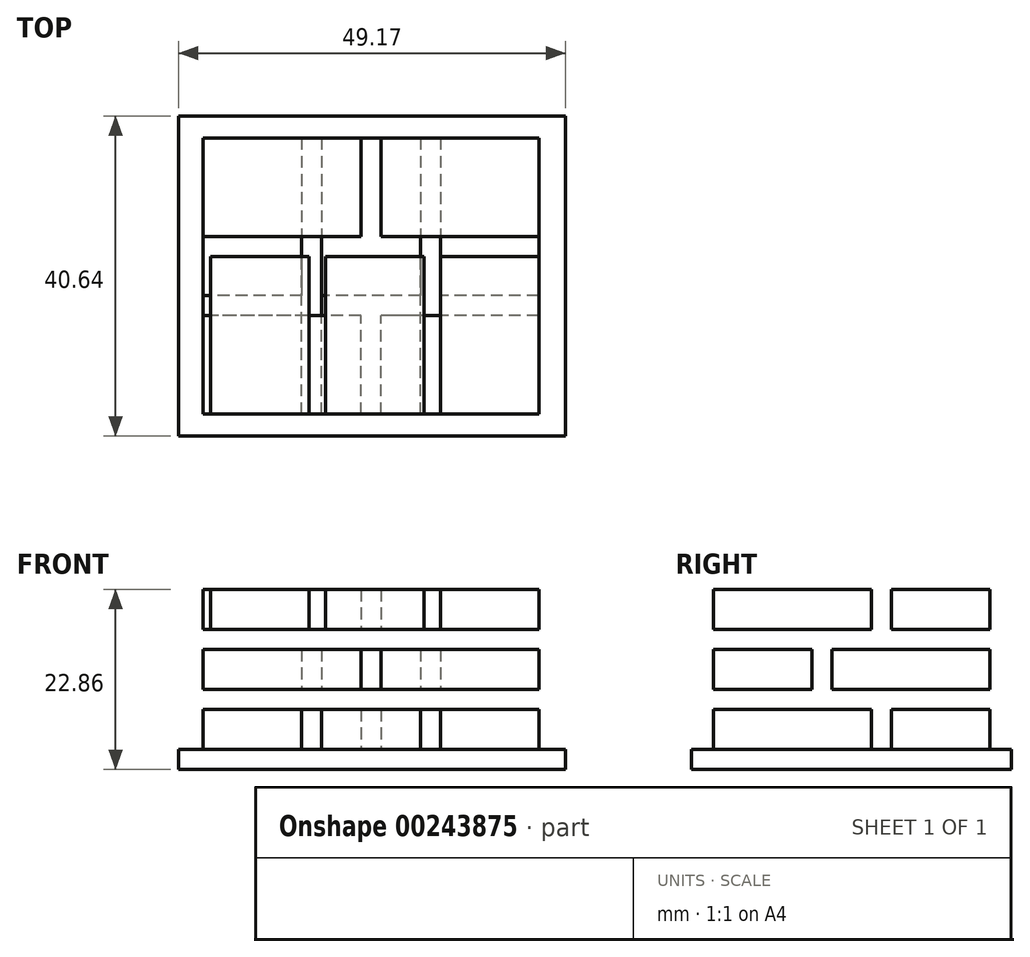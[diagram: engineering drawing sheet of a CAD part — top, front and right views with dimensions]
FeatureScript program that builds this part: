
annotation { "Feature Type Name" : "Feature", "Feature Type Description" : "" }
export const myFeature = defineFeature(function(context is Context, id is Id, definition is map)
    precondition{}
    {
        {
            var Q0;
            Q0=qCreatedBy(makeId("Top.planeOp"),FACE);
            var sketch = newSketch(context, id + "F0", { "sketchPlane" : qUnion([Q0])});
            skLineSegment(sketch, "E0.bottom", {"start": v(-21.31, 17.55) * mm, "end": v(-1.27, 17.55) * mm});
            skLineSegment(sketch, "E0.top", {"start": v(-21.31, 5.03) * mm, "end": v(-1.27, 5.03) * mm});
            skLineSegment(sketch, "E0.left", {"start": v(-21.31, 17.55) * mm, "end": v(-21.31, 5.03) * mm});
            skLineSegment(sketch, "E0.right", {"start": v(-1.27, 17.55) * mm, "end": v(-1.27, 5.03) * mm});
            skLineSegment(sketch, "E1.1.0.0", {"start": v(21.31, 17.55) * mm, "end": v(21.31, 5.03) * mm});
            skLineSegment(sketch, "E1.1.0.1", {"start": v(1.27, 17.55) * mm, "end": v(1.27, 5.03) * mm});
            skLineSegment(sketch, "E1.1.0.2", {"start": v(1.27, 5.03) * mm, "end": v(21.31, 5.03) * mm});
            skLineSegment(sketch, "E1.1.0.3", {"start": v(1.27, 17.55) * mm, "end": v(21.31, 17.55) * mm});
            skLineSegment(sketch, "E1.direction1", {"start": v(-21.31, 5.03) * mm, "end": v(1.27, 5.03) * mm, "construction": true});
            skLineSegment(sketch, "E2.bottom", {"start": v(-21.31, -17.55) * mm, "end": v(-21.31, 2.5) * mm});
            skLineSegment(sketch, "E2.top", {"start": v(-8.8, -17.55) * mm, "end": v(-8.8, 2.5) * mm});
            skLineSegment(sketch, "E2.left", {"start": v(-21.31, -17.55) * mm, "end": v(-8.8, -17.55) * mm});
            skLineSegment(sketch, "E2.right", {"start": v(-21.31, 2.5) * mm, "end": v(-8.8, 2.5) * mm});
            skLineSegment(sketch, "E3.1.0.0", {"start": v(-6.26, -17.55) * mm, "end": v(6.26, -17.55) * mm});
            skLineSegment(sketch, "E3.1.0.1", {"start": v(6.26, -17.55) * mm, "end": v(6.26, 2.5) * mm});
            skLineSegment(sketch, "E3.1.0.2", {"start": v(-6.26, -17.55) * mm, "end": v(-6.26, 2.5) * mm});
            skLineSegment(sketch, "E3.1.0.3", {"start": v(-6.26, 2.5) * mm, "end": v(6.26, 2.5) * mm});
            skLineSegment(sketch, "E3.2.0.0", {"start": v(8.8, -17.55) * mm, "end": v(21.31, -17.55) * mm});
            skLineSegment(sketch, "E3.2.0.1", {"start": v(21.31, -17.55) * mm, "end": v(21.31, 2.5) * mm});
            skLineSegment(sketch, "E3.2.0.2", {"start": v(8.8, -17.55) * mm, "end": v(8.8, 2.5) * mm});
            skLineSegment(sketch, "E3.2.0.3", {"start": v(8.8, 2.5) * mm, "end": v(21.31, 2.5) * mm});
            skLineSegment(sketch, "E3.direction1", {"start": v(-21.31, -17.55) * mm, "end": v(-6.26, -17.55) * mm, "construction": true});
            skLineSegment(sketch, "E4.bottom", {"start": v(-21.31, 17.55) * mm, "end": v(21.31, 17.55) * mm, "construction": true});
            skLineSegment(sketch, "E4.top", {"start": v(-21.31, -17.55) * mm, "end": v(21.31, -17.55) * mm, "construction": true});
            skLineSegment(sketch, "E4.left", {"start": v(-21.31, 17.55) * mm, "end": v(-21.31, -17.55) * mm, "construction": true});
            skLineSegment(sketch, "E4.right", {"start": v(21.31, 17.55) * mm, "end": v(21.31, -17.55) * mm, "construction": true});
            skSolve(sketch);
        }
        {
            var Q0;
            Q0=makeQuery(id+"F0.imprint","IMPRINT",FACE,{"disambiguationData":[TD([[makeQuery(id+"F0.imprint","IMPRINT",EDGE,{"derivedFrom":sQuery(id+"F0.wireOp",EDGE,"E1.1.0.0")}),-1.0]])]});
            var Q1;
            Q1=makeQuery(id+"F0.imprint","IMPRINT",FACE,{"disambiguationData":[TD([[makeQuery(id+"F0.imprint","IMPRINT",EDGE,{"derivedFrom":sQuery(id+"F0.wireOp",EDGE,"E3.2.0.0")}),1.0]])]});
            var Q2;
            Q2=makeQuery(id+"F0.imprint","IMPRINT",FACE,{"disambiguationData":[TD([[makeQuery(id+"F0.imprint","IMPRINT",EDGE,{"derivedFrom":sQuery(id+"F0.wireOp",EDGE,"E3.1.0.0")}),1.0]])]});
            var Q3;
            Q3=makeQuery(id+"F0.imprint","IMPRINT",FACE,{"disambiguationData":[TD([[makeQuery(id+"F0.imprint","IMPRINT",EDGE,{"derivedFrom":sQuery(id+"F0.wireOp",EDGE,"E2.bottom")}),-1.0]])]});
            var Q4;
            Q4=makeQuery(id+"F0.imprint","IMPRINT",FACE,{"disambiguationData":[TD([[makeQuery(id+"F0.imprint","IMPRINT",EDGE,{"derivedFrom":sQuery(id+"F0.wireOp",EDGE,"E0.bottom")}),-1.0]])]});
            extrude(context, id + "F1", {"entities" : qUnion([Q0, Q1, Q2, Q3, Q4]), "depth" : 5.08 * mm});
        }
        {
            var Q0;
            Q0=qCreatedBy(makeId("Front.planeOp"),FACE);
            var sketch = newSketch(context, id + "F2", { "sketchPlane" : qUnion([Q0])});
            skLineSegment(sketch, "E5.bottom", {"start": v(-24.44, 0) * mm, "end": v(24.73, 0) * mm});
            skLineSegment(sketch, "E5.top", {"start": v(-24.44, -2.54) * mm, "end": v(24.73, -2.54) * mm});
            skLineSegment(sketch, "E5.left", {"start": v(-24.44, 0) * mm, "end": v(-24.44, -2.54) * mm});
            skLineSegment(sketch, "E5.right", {"start": v(24.73, 0) * mm, "end": v(24.73, -2.54) * mm});
            skSolve(sketch);
        }
        {
            var Q0;
            Q0=makeQuery(id+"F2.imprint","IMPRINT",FACE,{"disambiguationData":[TD([[makeQuery(id+"F2.imprint","IMPRINT",EDGE,{"derivedFrom":sQuery(id+"F2.wireOp",EDGE,"E5.bottom")}),-1.0]])]});
            extrude(context, id + "F3", {"entities" : qUnion([Q0]), "endBound" : BoundingType.SYMMETRIC, "depth" : 40.64 * mm});
        }
        {
            var Q0;
            Q0=makeQuery(id+"F1.opExtrude","CAP_FACE",FACE,{"disambiguationData":[OSD([sQuery(id+"F0.wireOp",EDGE,"E0.bottom"),sQuery(id+"F0.wireOp",EDGE,"E0.top"),sQuery(id+"F0.wireOp",EDGE,"E0.left"),sQuery(id+"F0.wireOp",EDGE,"E0.right")])],"isStart":false});
            cPlane(context, id + "F4", {"entities" : qUnion([Q0]), "cplaneType" : CPlaneType.OFFSET, "offset" : 2.54 * mm, "width" : 152.4 * mm, "height" : 152.4 * mm});
        }
        {
            var Q0;
            Q0=qCreatedBy(id+"F4.planeOp",FACE);
            var sketch = newSketch(context, id + "F5", { "sketchPlane" : qUnion([Q0])});
            skLineSegment(sketch, "E6.bottom", {"start": v(21.31, -17.55) * mm, "end": v(1.27, -17.55) * mm});
            skLineSegment(sketch, "E6.top", {"start": v(21.31, -5.03) * mm, "end": v(1.27, -5.03) * mm});
            skLineSegment(sketch, "E6.left", {"start": v(21.31, -17.55) * mm, "end": v(21.31, -5.03) * mm});
            skLineSegment(sketch, "E6.right", {"start": v(1.27, -17.55) * mm, "end": v(1.27, -5.03) * mm});
            skLineSegment(sketch, "E7.1.0.0", {"start": v(-21.31, -17.55) * mm, "end": v(-21.31, -5.03) * mm});
            skLineSegment(sketch, "E7.1.0.1", {"start": v(-1.27, -17.55) * mm, "end": v(-1.27, -5.03) * mm});
            skLineSegment(sketch, "E7.1.0.2", {"start": v(-1.27, -5.03) * mm, "end": v(-21.31, -5.03) * mm});
            skLineSegment(sketch, "E7.1.0.3", {"start": v(-1.27, -17.55) * mm, "end": v(-21.31, -17.55) * mm});
            skLineSegment(sketch, "E7.direction1", {"start": v(21.31, -5.03) * mm, "end": v(-1.27, -5.03) * mm, "construction": true});
            skLineSegment(sketch, "E8.bottom", {"start": v(21.31, 17.55) * mm, "end": v(21.31, -2.5) * mm});
            skLineSegment(sketch, "E8.top", {"start": v(8.8, 17.55) * mm, "end": v(8.8, -2.5) * mm});
            skLineSegment(sketch, "E8.left", {"start": v(21.31, 17.55) * mm, "end": v(8.8, 17.55) * mm});
            skLineSegment(sketch, "E8.right", {"start": v(21.31, -2.5) * mm, "end": v(8.8, -2.5) * mm});
            skLineSegment(sketch, "E9.1.0.0", {"start": v(6.26, 17.55) * mm, "end": v(-6.26, 17.55) * mm});
            skLineSegment(sketch, "E9.1.0.1", {"start": v(-6.26, 17.55) * mm, "end": v(-6.26, -2.5) * mm});
            skLineSegment(sketch, "E9.1.0.2", {"start": v(6.26, 17.55) * mm, "end": v(6.26, -2.5) * mm});
            skLineSegment(sketch, "E9.1.0.3", {"start": v(6.26, -2.5) * mm, "end": v(-6.26, -2.5) * mm});
            skLineSegment(sketch, "E9.2.0.0", {"start": v(-8.8, 17.55) * mm, "end": v(-21.31, 17.55) * mm});
            skLineSegment(sketch, "E9.2.0.1", {"start": v(-21.31, 17.55) * mm, "end": v(-21.31, -2.5) * mm});
            skLineSegment(sketch, "E9.2.0.2", {"start": v(-8.8, 17.55) * mm, "end": v(-8.8, -2.5) * mm});
            skLineSegment(sketch, "E9.2.0.3", {"start": v(-8.8, -2.5) * mm, "end": v(-21.31, -2.5) * mm});
            skLineSegment(sketch, "E9.direction1", {"start": v(21.31, 17.55) * mm, "end": v(6.26, 17.55) * mm, "construction": true});
            skLineSegment(sketch, "E10.bottom", {"start": v(21.31, -17.55) * mm, "end": v(-21.31, -17.55) * mm, "construction": true});
            skLineSegment(sketch, "E10.top", {"start": v(21.31, 17.55) * mm, "end": v(-21.31, 17.55) * mm, "construction": true});
            skLineSegment(sketch, "E10.left", {"start": v(21.31, -17.55) * mm, "end": v(21.31, 17.55) * mm, "construction": true});
            skLineSegment(sketch, "E10.right", {"start": v(-21.31, -17.55) * mm, "end": v(-21.31, 17.55) * mm, "construction": true});
            skSolve(sketch);
        }
        {
            var Q0;
            {var subQ1=sQuery(id+"F5.wireOp",EDGE,"E9.1.0.2");Q0=makeQuery(id+"F5.imprint","IMPRINT",FACE,{"disambiguationData":[TD([[makeQuery(id+"F5.imprint","IMPRINT",EDGE,{"derivedFrom":subQ1}),-1.0]])]});}
            var Q1;
            {var subQ1=makeQuery(id+"F1.opExtrude","CAP_EDGE",EDGE,{"disambiguationData":[OSD([sQuery(id+"F0.wireOp",EDGE,"E0.right")])],"isStart":false});Q1=makeQuery(id+"F5.imprint","IMPRINT",FACE,{"disambiguationData":[TD([[makeQuery(id+"F5.imprint","IMPRINT",EDGE,{"derivedFrom":subQ1}),-1.0]])]});}
            var Q2;
            Q2=makeQuery(id+"F5.imprint","IMPRINT",FACE,{"disambiguationData":[TD([[makeQuery(id+"F5.imprint","IMPRINT",EDGE,{"derivedFrom":sQuery(id+"F5.wireOp",EDGE,"E8.bottom")}),-1.0]])]});
            var Q3;
            Q3=makeQuery(id+"F5.imprint","IMPRINT",FACE,{"disambiguationData":[TD([[makeQuery(id+"F5.imprint","IMPRINT",EDGE,{"derivedFrom":sQuery(id+"F5.wireOp",EDGE,"E6.bottom")}),-1.0]])]});
            var Q4;
            Q4=makeQuery(id+"F5.imprint","IMPRINT",FACE,{"disambiguationData":[TD([[makeQuery(id+"F5.imprint","IMPRINT",EDGE,{"derivedFrom":sQuery(id+"F5.wireOp",EDGE,"E7.1.0.0")}),-1.0]])]});
            var Q5;
            {var subQ3=sQuery(id+"F5.wireOp",EDGE,"E9.2.0.3");Q5=makeQuery(id+"F5.imprint","IMPRINT",FACE,{"disambiguationData":[TD([[makeQuery(id+"F5.imprint","IMPRINT",EDGE,{"derivedFrom":subQ3}),-1.0]])]});}
            var Q6;
            {var subQ0=sQuery(id+"F5.wireOp",EDGE,"E9.2.0.0");Q6=makeQuery(id+"F5.imprint","IMPRINT",FACE,{"disambiguationData":[TD([[makeQuery(id+"F5.imprint","IMPRINT",EDGE,{"derivedFrom":subQ0}),-1.0]])]});}
            extrude(context, id + "F6", {"entities" : qUnion([Q0, Q1, Q2, Q3, Q4, Q5, Q6]), "depth" : 5.08 * mm});
        }
        {
            var Q0;
            Q0=makeQuery(id+"F6.opExtrude","CAP_FACE",FACE,{"disambiguationData":[OSD([sQuery(id+"F5.wireOp",EDGE,"E9.2.0.0"),sQuery(id+"F5.wireOp",EDGE,"E9.2.0.1"),sQuery(id+"F5.wireOp",EDGE,"E9.2.0.2"),sQuery(id+"F5.wireOp",EDGE,"E9.2.0.3")])],"isStart":false});
            cPlane(context, id + "F7", {"entities" : qUnion([Q0]), "cplaneType" : CPlaneType.OFFSET, "offset" : 2.54 * mm, "width" : 152.4 * mm, "height" : 152.4 * mm});
        }
        {
            var Q0;
            Q0=qCreatedBy(id+"F7.planeOp",FACE);
            var sketch = newSketch(context, id + "F8", { "sketchPlane" : qUnion([Q0])});
            skLineSegment(sketch, "E11.bottom", {"start": v(-21.31, 17.55) * mm, "end": v(-1.27, 17.55) * mm});
            skLineSegment(sketch, "E11.top", {"start": v(-21.31, 5.03) * mm, "end": v(-1.27, 5.03) * mm});
            skLineSegment(sketch, "E11.left", {"start": v(-21.31, 17.55) * mm, "end": v(-21.31, 5.03) * mm});
            skLineSegment(sketch, "E11.right", {"start": v(-1.27, 17.55) * mm, "end": v(-1.27, 5.03) * mm});
            skLineSegment(sketch, "E12.1.0.0", {"start": v(21.31, 17.55) * mm, "end": v(21.31, 5.03) * mm});
            skLineSegment(sketch, "E12.1.0.1", {"start": v(1.27, 17.55) * mm, "end": v(1.27, 5.03) * mm});
            skLineSegment(sketch, "E12.1.0.2", {"start": v(1.27, 5.03) * mm, "end": v(21.31, 5.03) * mm});
            skLineSegment(sketch, "E12.1.0.3", {"start": v(1.27, 17.55) * mm, "end": v(21.31, 17.55) * mm});
            skLineSegment(sketch, "E12.direction1", {"start": v(-21.31, 5.03) * mm, "end": v(1.27, 5.03) * mm, "construction": true});
            skLineSegment(sketch, "E13.bottom", {"start": v(-20.4, -17.55) * mm, "end": v(-20.4, 2.5) * mm});
            skLineSegment(sketch, "E13.top", {"start": v(-7.88, -17.55) * mm, "end": v(-7.88, 2.5) * mm});
            skLineSegment(sketch, "E13.left", {"start": v(-20.4, -17.55) * mm, "end": v(-7.88, -17.55) * mm});
            skLineSegment(sketch, "E13.right", {"start": v(-20.4, 2.5) * mm, "end": v(-7.88, 2.5) * mm});
            skLineSegment(sketch, "E14.1.0.0", {"start": v(-5.8, -17.55) * mm, "end": v(6.72, -17.55) * mm});
            skLineSegment(sketch, "E14.1.0.1", {"start": v(6.72, -17.55) * mm, "end": v(6.72, 2.5) * mm});
            skLineSegment(sketch, "E14.1.0.2", {"start": v(-5.8, -17.55) * mm, "end": v(-5.8, 2.5) * mm});
            skLineSegment(sketch, "E14.1.0.3", {"start": v(-5.8, 2.5) * mm, "end": v(6.72, 2.5) * mm});
            skLineSegment(sketch, "E14.2.0.0", {"start": v(8.8, -17.55) * mm, "end": v(21.31, -17.55) * mm});
            skLineSegment(sketch, "E14.2.0.1", {"start": v(21.31, -17.55) * mm, "end": v(21.31, 2.5) * mm});
            skLineSegment(sketch, "E14.2.0.2", {"start": v(8.8, -17.55) * mm, "end": v(8.8, 2.5) * mm});
            skLineSegment(sketch, "E14.2.0.3", {"start": v(8.8, 2.5) * mm, "end": v(21.31, 2.5) * mm});
            skLineSegment(sketch, "E14.direction1", {"start": v(-20.4, -17.55) * mm, "end": v(-5.8, -17.55) * mm, "construction": true});
            skLineSegment(sketch, "E15.bottom", {"start": v(-21.31, 17.55) * mm, "end": v(21.31, 17.55) * mm, "construction": true});
            skLineSegment(sketch, "E15.top", {"start": v(-21.31, -17.55) * mm, "end": v(21.31, -17.55) * mm, "construction": true});
            skLineSegment(sketch, "E15.left", {"start": v(-21.31, 17.55) * mm, "end": v(-21.31, -17.55) * mm, "construction": true});
            skLineSegment(sketch, "E15.right", {"start": v(21.31, 17.55) * mm, "end": v(21.31, -17.55) * mm, "construction": true});
            skSolve(sketch);
        }
        {
            var Q0;
            Q0=makeQuery(id+"F8.imprint","IMPRINT",FACE,{"disambiguationData":[TD([[makeQuery(id+"F8.imprint","IMPRINT",EDGE,{"derivedFrom":sQuery(id+"F8.wireOp",EDGE,"E11.bottom")}),-1.0]])]});
            var Q1;
            Q1=makeQuery(id+"F8.imprint","IMPRINT",FACE,{"disambiguationData":[TD([[makeQuery(id+"F8.imprint","IMPRINT",EDGE,{"derivedFrom":sQuery(id+"F8.wireOp",EDGE,"E12.1.0.0")}),-1.0]])]});
            var Q2;
            Q2=makeQuery(id+"F8.imprint","IMPRINT",FACE,{"disambiguationData":[TD([[makeQuery(id+"F8.imprint","IMPRINT",EDGE,{"derivedFrom":sQuery(id+"F8.wireOp",EDGE,"E14.2.0.0")}),1.0]])]});
            var Q3;
            Q3=makeQuery(id+"F8.imprint","IMPRINT",FACE,{"disambiguationData":[TD([[makeQuery(id+"F8.imprint","IMPRINT",EDGE,{"derivedFrom":sQuery(id+"F8.wireOp",EDGE,"E14.1.0.0")}),1.0]])]});
            var Q4;
            Q4=makeQuery(id+"F8.imprint","IMPRINT",FACE,{"disambiguationData":[TD([[makeQuery(id+"F8.imprint","IMPRINT",EDGE,{"derivedFrom":sQuery(id+"F8.wireOp",EDGE,"E13.bottom")}),-1.0]])]});
            extrude(context, id + "F9", {"entities" : qUnion([Q0, Q1, Q2, Q3, Q4]), "depth" : 5.08 * mm});
        }
    });
